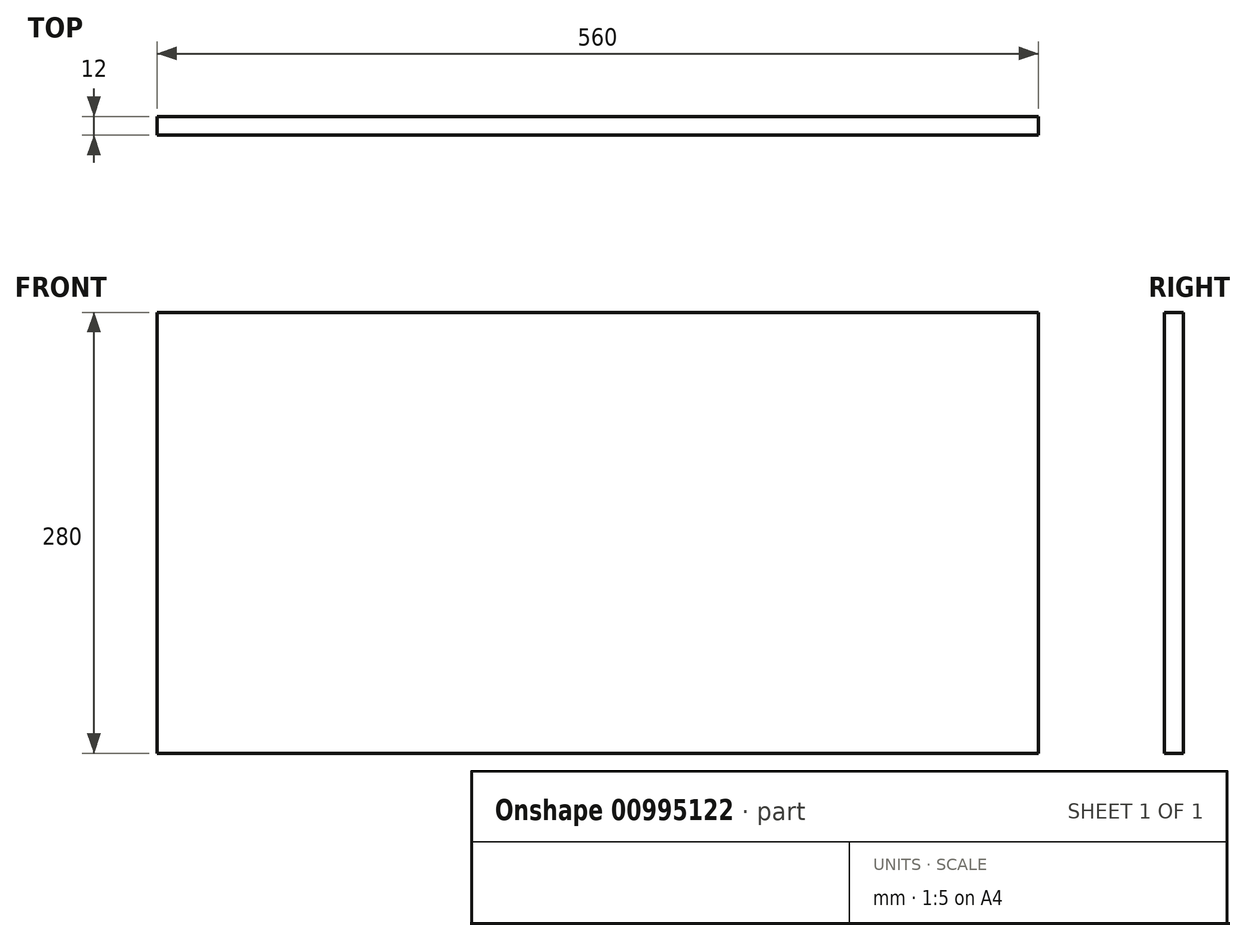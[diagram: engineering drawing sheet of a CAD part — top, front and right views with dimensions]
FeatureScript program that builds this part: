
annotation { "Feature Type Name" : "Feature", "Feature Type Description" : "" }
export const myFeature = defineFeature(function(context is Context, id is Id, definition is map)
    precondition{}
    {
        {
            var Q0;
            Q0=qCreatedBy(makeId("Front.planeOp"),FACE);
            var sketch = newSketch(context, id + "F0", { "sketchPlane" : qUnion([Q0])});
            skLineSegment(sketch, "E0", {"start": v(-380, 0) * mm, "end": v(-380, 350) * mm, "construction": true});
            skLineSegment(sketch, "E1", {"start": v(-380, 350) * mm, "end": v(0, 480) * mm, "construction": true});
            skLineSegment(sketch, "E2", {"start": v(0, 480) * mm, "end": v(380, 350) * mm, "construction": true});
            skLineSegment(sketch, "E3", {"start": v(380, 350) * mm, "end": v(380, 0) * mm, "construction": true});
            skLineSegment(sketch, "E4", {"start": v(380, 0) * mm, "end": v(280, 0) * mm, "construction": true});
            skLineSegment(sketch, "E5", {"start": v(280, 0) * mm, "end": v(280, 280) * mm});
            skLineSegment(sketch, "E6", {"start": v(280, 280) * mm, "end": v(-280, 280) * mm});
            skLineSegment(sketch, "E7", {"start": v(-280, 280) * mm, "end": v(-280, 0) * mm});
            skLineSegment(sketch, "E8", {"start": v(-280, 0) * mm, "end": v(-380, 0) * mm, "construction": true});
            skLineSegment(sketch, "E9", {"start": v(-280, 0) * mm, "end": v(280, 0) * mm});
            skSolve(sketch);
        }
        {
            var Q0;
            Q0=qSketchRegion(id+"F0",true);
            extrude(context, id + "F1", {"entities" : qUnion([Q0]), "depth" : 12 * mm, "offsetDistance" : 25 * mm});
        }
        {
            var Q0;
            Q0 = qSketchRegion(id + "F0", true);
            extrude(context, id + "F2", {"entities" : qUnion([Q0]), "operationType" : NewBodyOperationType.ADD, "depth" : 12 * mm, "offsetDistance" : 25 * mm});
        }
    });
